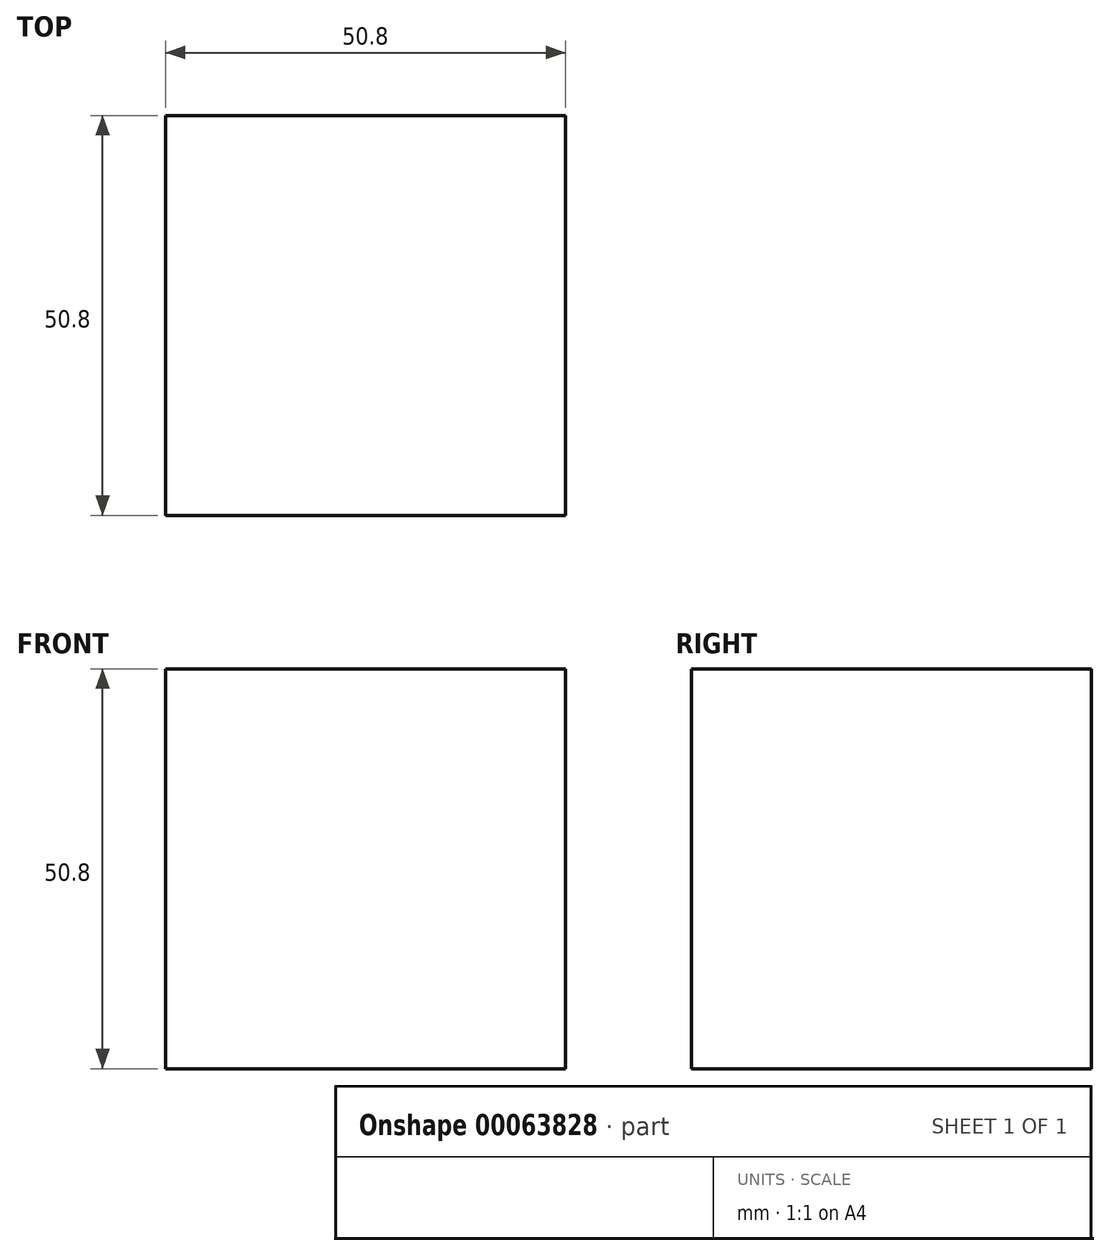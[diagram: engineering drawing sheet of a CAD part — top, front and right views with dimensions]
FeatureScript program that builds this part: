
annotation { "Feature Type Name" : "Feature", "Feature Type Description" : "" }
export const myFeature = defineFeature(function(context is Context, id is Id, definition is map)
    precondition{}
    {
        {
            var Q0;
            Q0=qCreatedBy(makeId("Front.planeOp"),FACE);
            var sketch = newSketch(context, id + "F0", { "sketchPlane" : qUnion([Q0])});
            skLineSegment(sketch, "E0.bottom", {"start": v(-50.8, 50.8) * mm, "end": v(0, 50.8) * mm});
            skLineSegment(sketch, "E0.top", {"start": v(-50.8, 0) * mm, "end": v(0, 0) * mm});
            skLineSegment(sketch, "E0.left", {"start": v(-50.8, 50.8) * mm, "end": v(-50.8, 0) * mm});
            skLineSegment(sketch, "E0.right", {"start": v(0, 50.8) * mm, "end": v(0, 0) * mm});
            skSolve(sketch);
        }
        {
            var Q0;
            Q0=makeQuery(id+"F0.imprint","IMPRINT",FACE,{"disambiguationData":[TD([[makeQuery(id+"F0.imprint","IMPRINT",EDGE,{"derivedFrom":sQuery(id+"F0.wireOp",EDGE,"E0.bottom")}),-1.0]])]});
            extrude(context, id + "F1", {"entities" : qUnion([Q0]), "depth" : 50.8 * mm, "hasDraft" : true, "draftAngle" : 0 * degree});
        }
    });
